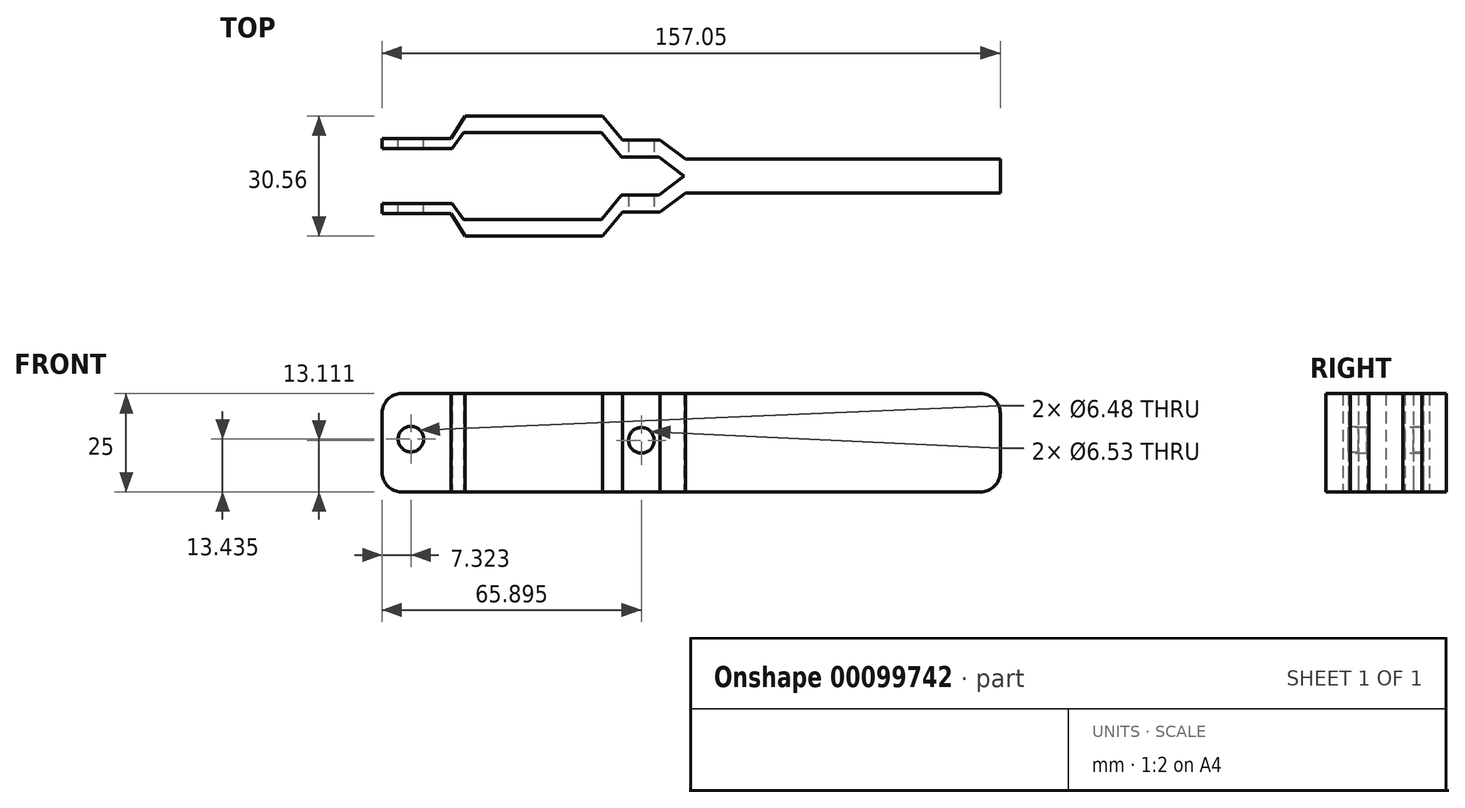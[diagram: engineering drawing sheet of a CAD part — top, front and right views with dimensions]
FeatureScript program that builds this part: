
annotation { "Feature Type Name" : "Feature", "Feature Type Description" : "" }
export const myFeature = defineFeature(function(context is Context, id is Id, definition is map)
    precondition{}
    {
        {
            var Q0;
            Q0=qCreatedBy(makeId("Top.planeOp"),FACE);
            var sketch = newSketch(context, id + "F0", { "sketchPlane" : qUnion([Q0])});
            skLineSegment(sketch, "E0", {"start": v(-16.66, -4.28) * mm, "end": v(55.34, -4.28) * mm});
            skLineSegment(sketch, "E1", {"start": v(-16.66, -4.28) * mm, "end": v(-23.06, -9.1) * mm});
            skLineSegment(sketch, "E2", {"start": v(-23.06, -9.1) * mm, "end": v(-32.58, -9.1) * mm});
            skLineSegment(sketch, "E3", {"start": v(-32.58, -9.1) * mm, "end": v(-37.65, -15.28) * mm});
            skLineSegment(sketch, "E4", {"start": v(-37.65, -15.28) * mm, "end": v(-72.65, -15.28) * mm});
            skLineSegment(sketch, "E5", {"start": v(-72.65, -15.28) * mm, "end": v(-76.14, -9.55) * mm});
            skLineSegment(sketch, "E6", {"start": v(-76.14, -9.55) * mm, "end": v(-93.71, -9.55) * mm});
            skLineSegment(sketch, "E7.MirrorCS", {"start": v(-37.65, 15.28) * mm, "end": v(-72.65, 15.28) * mm});
            skLineSegment(sketch, "E8.MirrorCS", {"start": v(-23.06, 9.1) * mm, "end": v(-32.58, 9.1) * mm});
            skLineSegment(sketch, "E9.MirrorCS", {"start": v(-16.66, 4.28) * mm, "end": v(-23.06, 9.1) * mm});
            skLineSegment(sketch, "E10.MirrorCS", {"start": v(-76.14, 9.55) * mm, "end": v(-93.71, 9.55) * mm});
            skLineSegment(sketch, "E11.MirrorCS", {"start": v(-72.65, 15.28) * mm, "end": v(-76.14, 9.55) * mm});
            skLineSegment(sketch, "E12.MirrorCS", {"start": v(-32.58, 9.1) * mm, "end": v(-37.65, 15.28) * mm});
            skLineSegment(sketch, "E13.MirrorCS", {"start": v(-16.66, 4.28) * mm, "end": v(55.34, 4.28) * mm});
            skLineSegment(sketch, "E14", {"start": v(55.34, 4.28) * mm, "end": v(63.34, 4.28) * mm});
            skLineSegment(sketch, "E15.MirrorCS", {"start": v(55.34, -4.28) * mm, "end": v(63.34, -4.28) * mm});
            skLineSegment(sketch, "E16", {"start": v(63.34, 4.28) * mm, "end": v(63.34, -4.28) * mm});
            skLineSegment(sketch, "E17", {"start": v(-17, 0) * mm, "end": v(-23.4, -4.81) * mm});
            skLineSegment(sketch, "E18", {"start": v(-23.4, -4.81) * mm, "end": v(-32.92, -4.81) * mm});
            skLineSegment(sketch, "E19", {"start": v(-32.92, -4.81) * mm, "end": v(-37.99, -11) * mm});
            skLineSegment(sketch, "E20", {"start": v(-37.99, -11) * mm, "end": v(-72.99, -11) * mm});
            skLineSegment(sketch, "E21", {"start": v(-72.99, -11) * mm, "end": v(-75.93, -7) * mm});
            skLineSegment(sketch, "E22", {"start": v(-75.93, -7) * mm, "end": v(-93.71, -7) * mm});
            skLineSegment(sketch, "E23.MirrorCS", {"start": v(-32.92, 4.81) * mm, "end": v(-37.99, 11) * mm});
            skLineSegment(sketch, "E24.MirrorCS", {"start": v(-75.93, 7) * mm, "end": v(-93.71, 7) * mm});
            skLineSegment(sketch, "E25.MirrorCS", {"start": v(-37.99, 11) * mm, "end": v(-72.99, 11) * mm});
            skLineSegment(sketch, "E26.MirrorCS", {"start": v(-23.4, 4.81) * mm, "end": v(-32.92, 4.81) * mm});
            skLineSegment(sketch, "E27.MirrorCS", {"start": v(-72.99, 11) * mm, "end": v(-75.93, 7) * mm});
            skLineSegment(sketch, "E28", {"start": v(-23.4, 4.81) * mm, "end": v(-17, 0) * mm});
            skLineSegment(sketch, "E29", {"start": v(-93.71, -7) * mm, "end": v(-93.71, -9.55) * mm});
            skLineSegment(sketch, "E30", {"start": v(-93.71, 7) * mm, "end": v(-93.71, 9.55) * mm});
            skLineSegment(sketch, "E31", {"start": v(-93.71, 7) * mm, "end": v(-101.12, 7) * mm});
            skLineSegment(sketch, "E32", {"start": v(-101.12, 7) * mm, "end": v(-101.12, 10.05) * mm});
            skSolve(sketch);
        }
        {
            var Q0;
            Q0 = qSketchRegion(id + "F0", true);
            extrude(context, id + "F1", {"entities" : qUnion([Q0]), "depth" : 25 * mm});
        }
        {
            var Q0;
            Q0=makeQuery(id+"F1.opExtrude","CAP_EDGE",EDGE,{"disambiguationData":[OSD([sQuery(id+"F0.wireOp",EDGE,"E16")])],"isStart":false});
            var Q1;
            Q1=makeQuery(id+"F1.opExtrude","CAP_EDGE",EDGE,{"disambiguationData":[OSD([sQuery(id+"F0.wireOp",EDGE,"E16")])],"isStart":true});
            fillet(context, id + "F2", {"entities" : qUnion([Q0, Q1]), "radius" : 5 * mm, "tangentPropagation" : true, "allowEdgeOverflow" : false});
        }
        {
            var Q0;
            Q0=makeQuery(id+"F1.opExtrude","CAP_EDGE",EDGE,{"disambiguationData":[OSD([sQuery(id+"F0.wireOp",EDGE,"E30")])],"isStart":false});
            var Q1;
            Q1=makeQuery(id+"F1.opExtrude","CAP_EDGE",EDGE,{"disambiguationData":[OSD([sQuery(id+"F0.wireOp",EDGE,"E30")])],"isStart":true});
            var Q2;
            Q2=makeQuery(id+"F1.opExtrude","CAP_EDGE",EDGE,{"disambiguationData":[OSD([sQuery(id+"F0.wireOp",EDGE,"E29")])],"isStart":false});
            var Q3;
            Q3=makeQuery(id+"F1.opExtrude","CAP_EDGE",EDGE,{"disambiguationData":[OSD([sQuery(id+"F0.wireOp",EDGE,"E29")])],"isStart":true});
            fillet(context, id + "F3", {"entities" : qUnion([Q0, Q1, Q2, Q3]), "radius" : 5 * mm, "tangentPropagation" : true, "allowEdgeOverflow" : false});
        }
        {
            var Q0;
            Q0=makeQuery(id+"F1.opExtrude","SWEPT_FACE",FACE,{"disambiguationData":[OSD([sQuery(id+"F0.wireOp",EDGE,"E6")])]});
            var sketch = newSketch(context, id + "F4", { "sketchPlane" : qUnion([Q0])});
            skCircle(sketch, "E33", {"center": v(-86.39, 13.44) * mm, "radius": 3.24 * mm});
            skSolve(sketch);
        }
        {
            var Q0;
            Q0 = qSketchRegion(id + "F4", true);
            extrude(context, id + "F5", {"entities" : qUnion([Q0]), "operationType" : NewBodyOperationType.REMOVE, "depth" : 25 * mm, "hasSecondDirection" : true, "secondDirectionOppositeDirection" : true, "secondDirectionDepth" : 25 * mm});
        }
        {
            var Q0;
            Q0=qCreatedBy(makeId("Front.planeOp"),FACE);
            var sketch = newSketch(context, id + "F6", { "sketchPlane" : qUnion([Q0])});
            skCircle(sketch, "E34", {"center": v(-27.82, 13.11) * mm, "radius": 3.27 * mm});
            skSolve(sketch);
        }
        {
            var Q0;
            Q0 = qSketchRegion(id + "F6", true);
            extrude(context, id + "F7", {"entities" : qUnion([Q0]), "operationType" : NewBodyOperationType.REMOVE, "oppositeDirection" : true, "depth" : 25 * mm, "hasSecondDirection" : true, "secondDirectionOppositeDirection" : false, "secondDirectionDepth" : 25 * mm});
        }
    });
